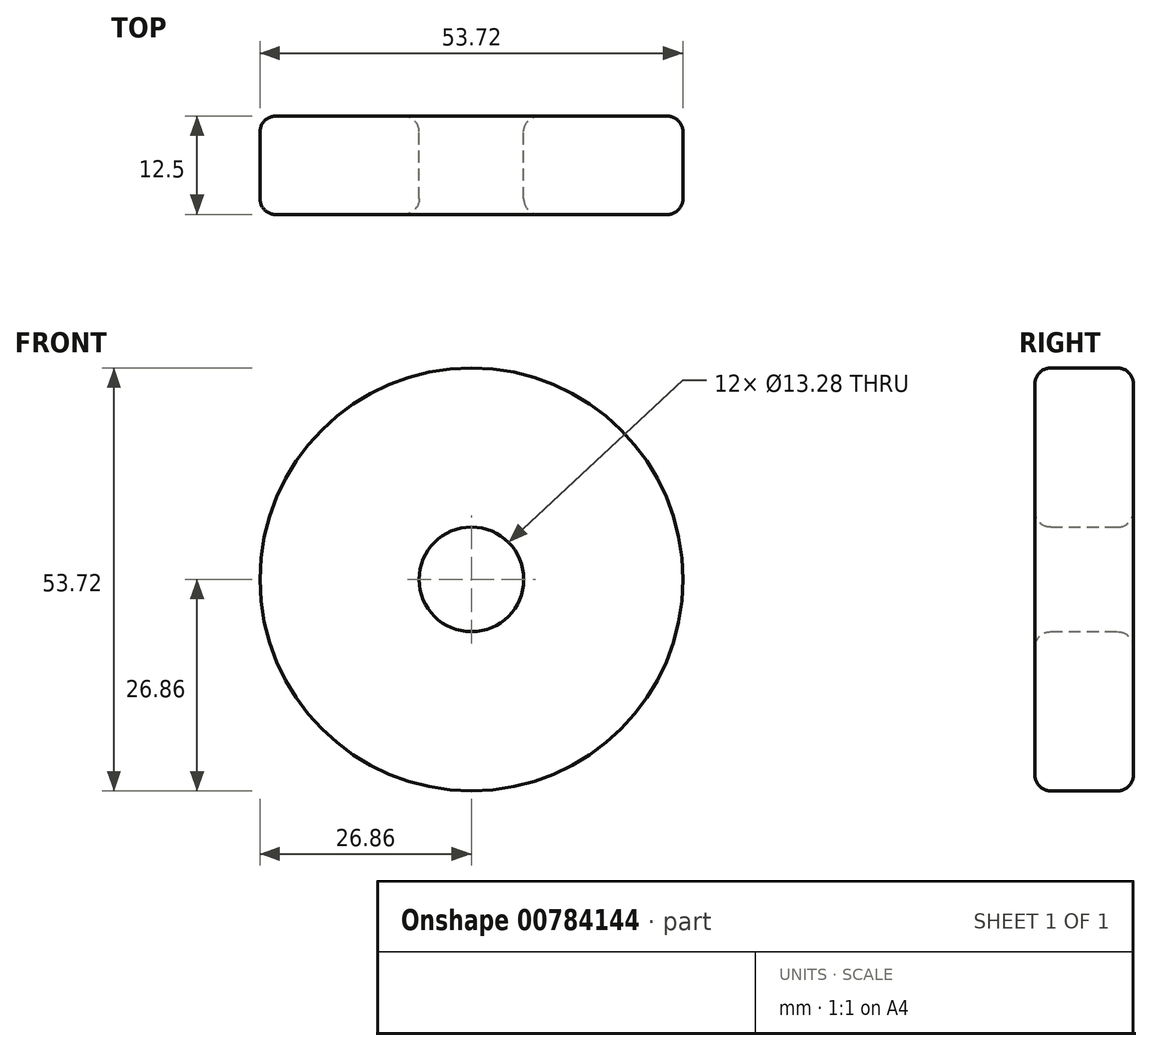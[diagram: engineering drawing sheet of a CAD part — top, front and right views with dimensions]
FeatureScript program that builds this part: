
annotation { "Feature Type Name" : "Feature", "Feature Type Description" : "" }
export const myFeature = defineFeature(function(context is Context, id is Id, definition is map)
    precondition{}
    {
        {
            var Q0;
            Q0=qCreatedBy(makeId("Front.planeOp"),FACE);
            var sketch = newSketch(context, id + "F0", { "sketchPlane" : qUnion([Q0])});
            skCircle(sketch, "E0", {"center": v(0, 0) * mm, "radius": 26.86 * mm});
            skCircle(sketch, "E1", {"center": v(0, 0) * mm, "radius": 29.34 * mm, "construction": true});
            skCircle(sketch, "E2", {"center": v(0, 0) * mm, "radius": 31.75 * mm, "construction": true});
            skLineSegment(sketch, "E3", {"start": v(0, 0) * mm, "end": v(0, 118.64) * mm});
            skLineSegment(sketch, "E4", {"start": v(0, 0) * mm, "end": v(-8.6, 131.21) * mm, "construction": true});
            skLineSegment(sketch, "E5", {"start": v(0, 29.34) * mm, "end": v(-49.7, 27.82) * mm, "construction": true});
            skLineSegment(sketch, "E6", {"start": v(0, 29.34) * mm, "end": v(-55.04, 7.37) * mm, "construction": true});
            skCircle(sketch, "E7", {"center": v(0, 0) * mm, "radius": 27.25 * mm, "construction": true});
            skCircle(sketch, "E8", {"center": v(0, 29.34) * mm, "radius": 14.6 * mm, "construction": true});
            skCircle(sketch, "E9", {"center": v(-13.57, 23.92) * mm, "radius": 14.6 * mm, "construction": true});
            skArc(sketch, "E10.MirrorCS", {"start": v(-3.71, 31.6) * mm, "mid": v(-2.74, 34.27) * mm, "end": v(-1.28, 36.72) * mm});
            skArc(sketch, "E11.MirrorCS", {"start": v(-4.09, 26.55) * mm, "mid": v(-4.13, 29.1) * mm, "end": v(-3.71, 31.6) * mm});
            skArc(sketch, "E12.MirrorCS", {"start": v(4.09, 26.55) * mm, "mid": v(4.13, 29.1) * mm, "end": v(3.71, 31.6) * mm});
            skArc(sketch, "E13.MirrorCS", {"start": v(3.71, 31.6) * mm, "mid": v(2.74, 34.27) * mm, "end": v(1.28, 36.72) * mm});
            skArc(sketch, "E14", {"start": v(1.28, 36.72) * mm, "mid": v(0, 36.78) * mm, "end": v(-1.28, 36.72) * mm});
            skCircle(sketch, "E15", {"center": v(0, 0) * mm, "radius": 6.64 * mm});
            skSolve(sketch);
        }
        {
            var Q0;
            Q0=makeQuery(id+"F0.imprint","IMPRINT",FACE,{"disambiguationData":[TD([[makeQuery(id+"F0.imprint","IMPRINT",EDGE,{"derivedFrom":sQuery(id+"F0.wireOp",EDGE,"E0")}),1.0]])]});
            var Q1;
            {var subQ1=sQuery(id+"F0.wireOp",EDGE,"E12.MirrorCS");Q1=makeQuery(id+"F0.imprint","IMPRINT",FACE,{"disambiguationData":[TD([[makeQuery(id+"F0.imprint","IMPRINT",EDGE,{"derivedFrom":subQ1}),1.0]])]});}
            var Q2;
            {var subQ1=sQuery(id+"F0.wireOp",EDGE,"E10.MirrorCS");Q2=makeQuery(id+"F0.imprint","IMPRINT",FACE,{"disambiguationData":[TD([[makeQuery(id+"F0.imprint","IMPRINT",EDGE,{"derivedFrom":subQ1}),-1.0]])]});}
            extrude(context, id + "F1", {"entities" : qUnion([Q0, Q1, Q2]), "depth" : 12.5 * mm, "offsetDistance" : 25 * mm});
        }
        {
            var Q0;
            Q0=makeQuery(id+"F1.opExtrude","SWEPT_BODY",BODY,{"disambiguationData":[OSD([sQuery(id+"F0.wireOp",EDGE,"E0"),sQuery(id+"F0.wireOp",EDGE,"onl3Hth0-gvNS-kGqj-OB4F-fPL2V5tkwlhU"),sQuery(id+"F0.wireOp",EDGE,"Q7TL4sB1-JfUO-6OG0-7ycH-ombt73yvZKSY"),sQuery(id+"F0.wireOp",EDGE,"1a21c05e-9d09-42d3-9229-0e8c2e2fe4b00.MirrorCS"),sQuery(id+"F0.wireOp",EDGE,"eaa4ace3-1fc1-4a64-ab22-bd398715a6fd0.MirrorCS"),sQuery(id+"F0.wireOp",EDGE,"L3lFsfQe-XlbY-od9d-117T-vAVvETbIJ5JL")])]});
            var Q1;
            Q1=makeQuery(id+"F1.opExtrude","SWEPT_FACE",FACE,{"disambiguationData":[OSD([sQuery(id+"F0.wireOp",EDGE,"E0")])]});
            circularPattern(context, id + "F2", {"entities" : qUnion([Q0]), "axis" : qUnion([Q1]), "angle" : 360 * degree, "instanceCount" : 12, "equalSpace" : true});
        }
        {
            var Q0;
            {var subQ0=sQuery(id+"F0.wireOp",EDGE,"CsDdt6R3-16vf-vRs4-WTDT-ATd0tmtERu7S");var subQ1=makeQuery(id+"F1.opExtrude","CAP_FACE",FACE,{"disambiguationData":[OSD([sQuery(id+"F0.wireOp",EDGE,"E0"),sQuery(id+"F0.wireOp",EDGE,"onl3Hth0-gvNS-kGqj-OB4F-fPL2V5tkwlhU"),sQuery(id+"F0.wireOp",EDGE,"Q7TL4sB1-JfUO-6OG0-7ycH-ombt73yvZKSY"),sQuery(id+"F0.wireOp",EDGE,"1a21c05e-9d09-42d3-9229-0e8c2e2fe4b00.MirrorCS"),sQuery(id+"F0.wireOp",EDGE,"eaa4ace3-1fc1-4a64-ab22-bd398715a6fd0.MirrorCS"),sQuery(id+"F0.wireOp",EDGE,"L3lFsfQe-XlbY-od9d-117T-vAVvETbIJ5JL"),subQ0])],"isStart":true});Q0=makeQuery(id+"F0dvbCyqXqC9UEo_1.boolean.opBoolean","MERGE",FACE,{"derivedFrom":[subQ1,makeQuery(id+"F2.opPattern","COPY",FACE,{"derivedFrom":subQ1,"instanceName":"1"}),makeQuery(id+"F2.opPattern","COPY",FACE,{"derivedFrom":subQ1,"instanceName":"2"}),makeQuery(id+"F2.opPattern","COPY",FACE,{"derivedFrom":subQ1,"instanceName":"3"}),makeQuery(id+"F2.opPattern","COPY",FACE,{"derivedFrom":subQ1,"instanceName":"4"}),makeQuery(id+"F2.opPattern","COPY",FACE,{"derivedFrom":subQ1,"instanceName":"5"}),makeQuery(id+"F2.opPattern","COPY",FACE,{"derivedFrom":subQ1,"instanceName":"6"}),makeQuery(id+"F2.opPattern","COPY",FACE,{"derivedFrom":subQ1,"instanceName":"7"}),makeQuery(id+"F2.opPattern","COPY",FACE,{"derivedFrom":subQ1,"instanceName":"8"}),makeQuery(id+"F2.opPattern","COPY",FACE,{"derivedFrom":subQ1,"instanceName":"9"}),makeQuery(id+"F2.opPattern","COPY",FACE,{"derivedFrom":subQ1,"instanceName":"10"}),makeQuery(id+"F2.opPattern","COPY",FACE,{"derivedFrom":subQ1,"instanceName":"11"}),makeQuery(id+"F2.opPattern","COPY",FACE,{"derivedFrom":subQ1,"instanceName":"12"}),makeQuery(id+"F2.opPattern","COPY",FACE,{"derivedFrom":subQ1,"instanceName":"13"}),makeQuery(id+"F2.opPattern","COPY",FACE,{"derivedFrom":subQ1,"instanceName":"14"}),makeQuery(id+"F2.opPattern","COPY",FACE,{"derivedFrom":subQ1,"instanceName":"15"}),makeQuery(id+"F2.opPattern","COPY",FACE,{"derivedFrom":subQ1,"instanceName":"16"}),makeQuery(id+"F2.opPattern","COPY",FACE,{"derivedFrom":subQ1,"instanceName":"17"}),makeQuery(id+"F2.opPattern","COPY",FACE,{"derivedFrom":subQ1,"instanceName":"18"}),makeQuery(id+"F2.opPattern","COPY",FACE,{"derivedFrom":subQ1,"instanceName":"19"}),makeQuery(id+"F2.opPattern","COPY",FACE,{"derivedFrom":subQ1,"instanceName":"20"}),makeQuery(id+"F2.opPattern","COPY",FACE,{"derivedFrom":subQ1,"instanceName":"21"}),makeQuery(id+"F2.opPattern","COPY",FACE,{"derivedFrom":subQ1,"instanceName":"22"}),makeQuery(id+"F2.opPattern","COPY",FACE,{"derivedFrom":subQ1,"instanceName":"23"}),makeQuery(id+"F0dvbCyqXqC9UEo_1.opExtrude","CAP_FACE",FACE,{"disambiguationData":[OSD([subQ0,sQuery(id+"F0.wireOp",EDGE,"54e66a6d-a6ab-4272-a859-17db4063e6c3.0"),sQuery(id+"F0.wireOp",EDGE,"54e66a6d-a6ab-4272-a859-17db4063e6c3.1"),sQuery(id+"F0.wireOp",EDGE,"54e66a6d-a6ab-4272-a859-17db4063e6c3.2"),sQuery(id+"F0.wireOp",EDGE,"54e66a6d-a6ab-4272-a859-17db4063e6c3.3"),sQuery(id+"F0.wireOp",EDGE,"54e66a6d-a6ab-4272-a859-17db4063e6c3.4"),sQuery(id+"F0.wireOp",EDGE,"54e66a6d-a6ab-4272-a859-17db4063e6c3.5")])],"isStart":true})]});}
            var Q1;
            {var subQ0=makeQuery(id+"F1.opExtrude","CAP_FACE",FACE,{"disambiguationData":[OSD([sQuery(id+"F0.wireOp",EDGE,"E0"),sQuery(id+"F0.wireOp",EDGE,"onl3Hth0-gvNS-kGqj-OB4F-fPL2V5tkwlhU"),sQuery(id+"F0.wireOp",EDGE,"Q7TL4sB1-JfUO-6OG0-7ycH-ombt73yvZKSY"),sQuery(id+"F0.wireOp",EDGE,"1a21c05e-9d09-42d3-9229-0e8c2e2fe4b00.MirrorCS"),sQuery(id+"F0.wireOp",EDGE,"eaa4ace3-1fc1-4a64-ab22-bd398715a6fd0.MirrorCS"),sQuery(id+"F0.wireOp",EDGE,"L3lFsfQe-XlbY-od9d-117T-vAVvETbIJ5JL"),sQuery(id+"F0.wireOp",EDGE,"CsDdt6R3-16vf-vRs4-WTDT-ATd0tmtERu7S")])],"isStart":false});Q1=makeQuery(id+"F0dvbCyqXqC9UEo_1.boolean.opBoolean","MERGE",FACE,{"derivedFrom":[subQ0,makeQuery(id+"F2.opPattern","COPY",FACE,{"derivedFrom":subQ0,"instanceName":"1"}),makeQuery(id+"F2.opPattern","COPY",FACE,{"derivedFrom":subQ0,"instanceName":"2"}),makeQuery(id+"F2.opPattern","COPY",FACE,{"derivedFrom":subQ0,"instanceName":"3"}),makeQuery(id+"F2.opPattern","COPY",FACE,{"derivedFrom":subQ0,"instanceName":"4"}),makeQuery(id+"F2.opPattern","COPY",FACE,{"derivedFrom":subQ0,"instanceName":"5"}),makeQuery(id+"F2.opPattern","COPY",FACE,{"derivedFrom":subQ0,"instanceName":"6"}),makeQuery(id+"F2.opPattern","COPY",FACE,{"derivedFrom":subQ0,"instanceName":"7"}),makeQuery(id+"F2.opPattern","COPY",FACE,{"derivedFrom":subQ0,"instanceName":"8"}),makeQuery(id+"F2.opPattern","COPY",FACE,{"derivedFrom":subQ0,"instanceName":"9"}),makeQuery(id+"F2.opPattern","COPY",FACE,{"derivedFrom":subQ0,"instanceName":"10"}),makeQuery(id+"F2.opPattern","COPY",FACE,{"derivedFrom":subQ0,"instanceName":"11"}),makeQuery(id+"F2.opPattern","COPY",FACE,{"derivedFrom":subQ0,"instanceName":"12"}),makeQuery(id+"F2.opPattern","COPY",FACE,{"derivedFrom":subQ0,"instanceName":"13"}),makeQuery(id+"F2.opPattern","COPY",FACE,{"derivedFrom":subQ0,"instanceName":"14"}),makeQuery(id+"F2.opPattern","COPY",FACE,{"derivedFrom":subQ0,"instanceName":"15"}),makeQuery(id+"F2.opPattern","COPY",FACE,{"derivedFrom":subQ0,"instanceName":"16"}),makeQuery(id+"F2.opPattern","COPY",FACE,{"derivedFrom":subQ0,"instanceName":"17"}),makeQuery(id+"F2.opPattern","COPY",FACE,{"derivedFrom":subQ0,"instanceName":"18"}),makeQuery(id+"F2.opPattern","COPY",FACE,{"derivedFrom":subQ0,"instanceName":"19"}),makeQuery(id+"F2.opPattern","COPY",FACE,{"derivedFrom":subQ0,"instanceName":"20"}),makeQuery(id+"F2.opPattern","COPY",FACE,{"derivedFrom":subQ0,"instanceName":"21"}),makeQuery(id+"F2.opPattern","COPY",FACE,{"derivedFrom":subQ0,"instanceName":"22"}),makeQuery(id+"F2.opPattern","COPY",FACE,{"derivedFrom":subQ0,"instanceName":"23"})]});}
            fillet(context, id + "F3", {"entities" : qUnion([Q0, Q1]), "radius" : 2 * mm, "tangentPropagation" : true, "allowEdgeOverflow" : false});
        }
    });
